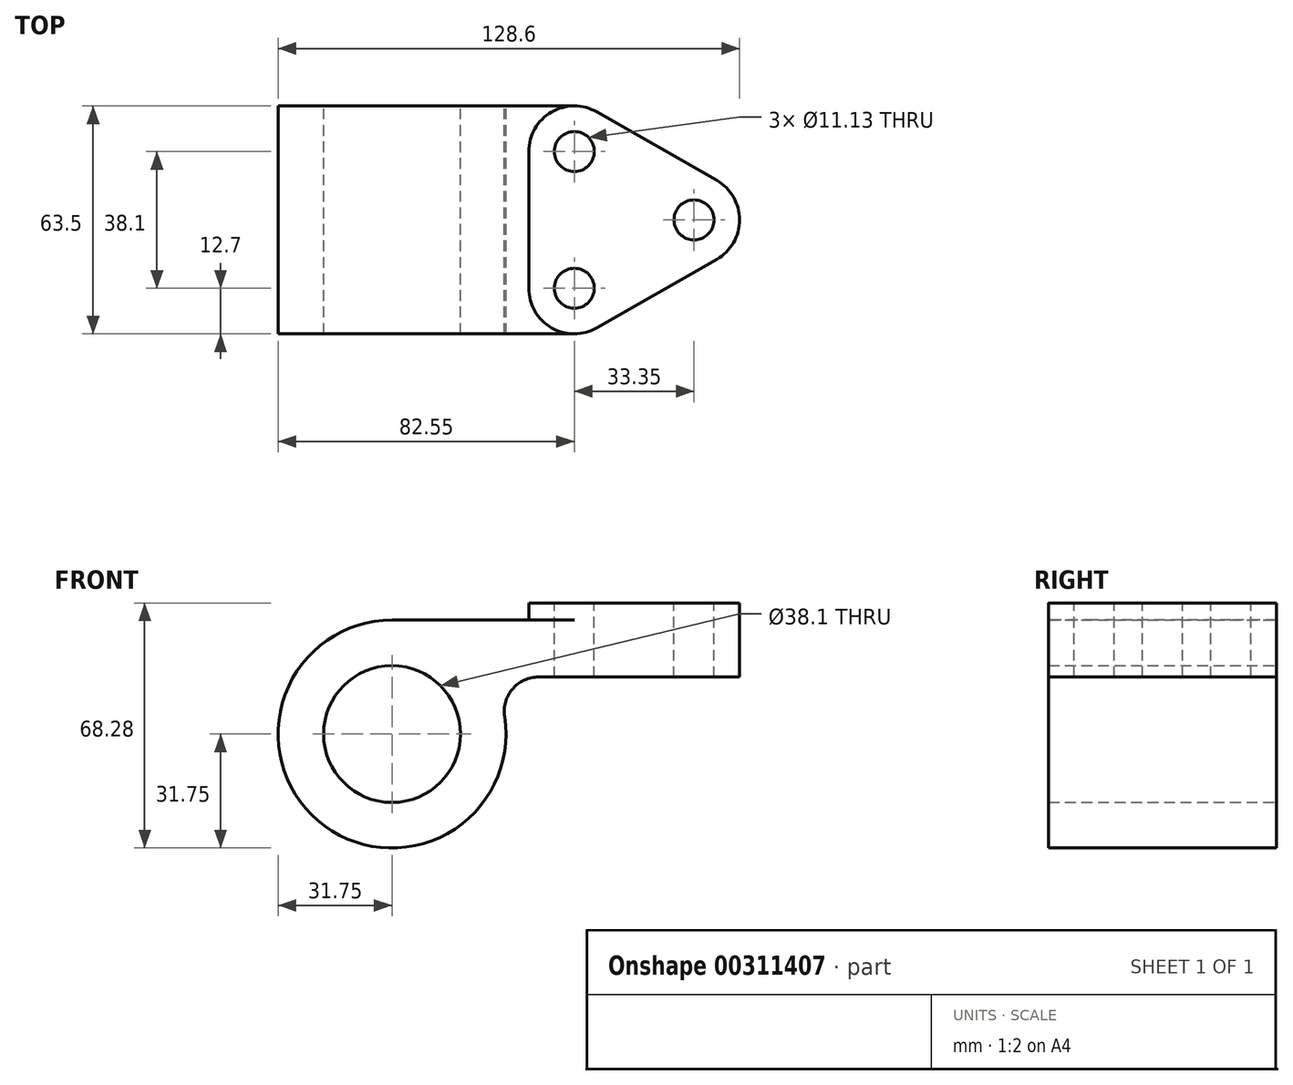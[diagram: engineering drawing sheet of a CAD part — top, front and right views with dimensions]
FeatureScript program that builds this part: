
annotation { "Feature Type Name" : "Feature", "Feature Type Description" : "" }
export const myFeature = defineFeature(function(context is Context, id is Id, definition is map)
    precondition{}
    {
        {
            var Q0;
            Q0=qCreatedBy(makeId("Front.planeOp"),FACE);
            var sketch = newSketch(context, id + "F0", { "sketchPlane" : qUnion([Q0])});
            skCircle(sketch, "E0", {"center": v(0, 0) * mm, "radius": 19.05 * mm});
            skLineSegment(sketch, "E1", {"start": v(0, 31.75) * mm, "end": v(50.8, 31.75) * mm});
            skArc(sketch, "E2", {"start": v(0, 31.75) * mm, "mid": v(-20.65, -24.12) * mm, "end": v(31.37, 4.88) * mm});
            skArc(sketch, "E3", {"start": v(31.37, 4.88) * mm, "mid": v(33.55, 12.55) * mm, "end": v(40.78, 15.87) * mm});
            skLineSegment(sketch, "E4", {"start": v(20.03, -24.63) * mm, "end": v(69.85, 15.87) * mm});
            skLineSegment(sketch, "E5", {"start": v(40.78, 15.87) * mm, "end": v(69.85, 15.87) * mm});
            skLineSegment(sketch, "E6", {"start": v(50.8, 31.75) * mm, "end": v(50.8, 15.87) * mm});
            skPoint(sketch, "E7", {"position": v(55.32, 15.87) * mm});
            skSolve(sketch);
        }
        {
            var Q0;
            Q0=makeQuery(id+"F0.imprint","IMPRINT",FACE,{"disambiguationData":[TD([[makeQuery(id+"F0.imprint","IMPRINT",EDGE,{"derivedFrom":sQuery(id+"F0.wireOp",EDGE,"E0")}),-1.0]])]});
            extrude(context, id + "F1", {"entities" : qUnion([Q0]), "depth" : 63.5 * mm, "symmetric" : true});
        }
        {
            var Q0;
            {var subQ1=sQuery(id+"F0.wireOp",EDGE,"E3");Q0=makeQuery(id+"F0.imprint","IMPRINT",FACE,{"disambiguationData":[TD([[makeQuery(id+"F0.imprint","IMPRINT",EDGE,{"derivedFrom":subQ1}),-1.0]])]});}
            extrude(context, id + "F2", {"entities" : qUnion([Q0]), "operationType" : NewBodyOperationType.ADD, "depth" : 9.52 * mm, "symmetric" : true});
        }
        {
            var Q0;
            Q0=makeQuery(id+"F1.opExtrude","SWEPT_FACE",FACE,{"disambiguationData":[OSD([sQuery(id+"F0.wireOp",EDGE,"E1")])]});
            var sketch = newSketch(context, id + "F3", { "sketchPlane" : qUnion([Q0])});
            skLineSegment(sketch, "E8.0.0", {"start": v(50.8, 31.75) * mm, "end": v(0, 31.75) * mm});
            skLineSegment(sketch, "E8.0.1", {"start": v(0, 31.75) * mm, "end": v(0, -31.75) * mm});
            skLineSegment(sketch, "E8.0.2", {"start": v(0, -31.75) * mm, "end": v(50.8, -31.75) * mm});
            skLineSegment(sketch, "E8.0.3", {"start": v(50.8, -31.75) * mm, "end": v(50.8, 31.75) * mm});
            skLineSegment(sketch, "E9", {"start": v(90.45, 11.03) * mm, "end": v(57.1, 30.08) * mm});
            skLineSegment(sketch, "E10", {"start": v(90.45, -11.03) * mm, "end": v(57.1, -30.08) * mm});
            skLineSegment(sketch, "E11", {"start": v(38.1, 19.05) * mm, "end": v(38.1, -19.05) * mm});
            skArc(sketch, "E12", {"start": v(38.1, 19.05) * mm, "mid": v(44.42, 30.03) * mm, "end": v(57.1, 30.08) * mm});
            skArc(sketch, "E13", {"start": v(90.45, 11.03) * mm, "mid": v(96.85, 0) * mm, "end": v(90.45, -11.03) * mm});
            skArc(sketch, "E14", {"start": v(38.1, -19.05) * mm, "mid": v(44.42, -30.03) * mm, "end": v(57.1, -30.08) * mm});
            skCircle(sketch, "E15", {"center": v(84.15, 0) * mm, "radius": 5.56 * mm});
            skCircle(sketch, "E16", {"center": v(50.8, -19.05) * mm, "radius": 5.56 * mm});
            skCircle(sketch, "E17", {"center": v(50.8, 19.05) * mm, "radius": 5.56 * mm});
            skLineSegment(sketch, "E18", {"start": v(0, 0) * mm, "end": v(101.92, 0) * mm, "construction": true});
            skSolve(sketch);
        }
        {
            var Q0;
            {var subQ6=sQuery(id+"F3.wireOp",EDGE,"E9");Q0=makeQuery(id+"F3.imprint","IMPRINT",FACE,{"disambiguationData":[TD([[makeQuery(id+"F3.imprint","IMPRINT",EDGE,{"derivedFrom":subQ6}),1.0]])]});}
            var Q1;
            {var subQ5=sQuery(id+"F3.wireOp",EDGE,"E11");Q1=makeQuery(id+"F3.imprint","IMPRINT",FACE,{"disambiguationData":[TD([[makeQuery(id+"F3.imprint","IMPRINT",EDGE,{"derivedFrom":subQ5}),1.0]])]});}
            var Q2;
            {var subQ0=sQuery(id+"F0.wireOp",EDGE,"E5");var subQ1=sQuery(id+"F0.wireOp",EDGE,"E3");var subQ2=sQuery(id+"F0.wireOp",EDGE,"E2");Q2=makeQuery(id+"F2.boolean.opBoolean","SPLIT",FACE,{"disambiguationData":[TD([makeQuery(id+"F2.opExtrude","CAP_FACE",FACE,{"disambiguationData":[OSD([subQ2,subQ1,sQuery(id+"F0.wireOp",EDGE,"E4"),subQ0])],"isStart":false})])],"derivedFrom":makeQuery(id+"F1.opExtrude","SWEPT_FACE",FACE,{"disambiguationData":[OSD([subQ0])]})});}
            extrude(context, id + "F4", {"entities" : qUnion([Q0, Q1]), "operationType" : NewBodyOperationType.ADD, "endBound" : BoundingType.UP_TO_SURFACE, "oppositeDirection" : true, "endBoundEntityFace" : qUnion([Q2]), "depth" : 25.4 * mm, "hasSecondDirection" : true, "secondDirectionOppositeDirection" : false, "secondDirectionDepth" : 4.78 * mm});
        }
        {
            var Q0;
            Q0=makeQuery(id+"F4.boolean.opBoolean","SPLIT",FACE,{"disambiguationData":[TD([makeQuery(id+"F4.opExtrude","SWEPT_FACE",FACE,{"disambiguationData":[OSD([sQuery(id+"F3.wireOp",EDGE,"E16")])]})])],"derivedFrom":makeQuery(id+"F1.opExtrude","SWEPT_FACE",FACE,{"disambiguationData":[OSD([sQuery(id+"F0.wireOp",EDGE,"E1")])]})});
            var Q1;
            Q1=makeQuery(id+"F4.boolean.opBoolean","SPLIT",FACE,{"disambiguationData":[TD([makeQuery(id+"F4.opExtrude","SWEPT_FACE",FACE,{"disambiguationData":[OSD([sQuery(id+"F3.wireOp",EDGE,"E17")])]})])],"derivedFrom":makeQuery(id+"F1.opExtrude","SWEPT_FACE",FACE,{"disambiguationData":[OSD([sQuery(id+"F0.wireOp",EDGE,"E1")])]})});
            extrude(context, id + "F5", {"entities" : qUnion([Q0, Q1]), "operationType" : NewBodyOperationType.REMOVE, "endBound" : BoundingType.THROUGH_ALL, "oppositeDirection" : true, "depth" : 25.4 * mm});
        }
    });
